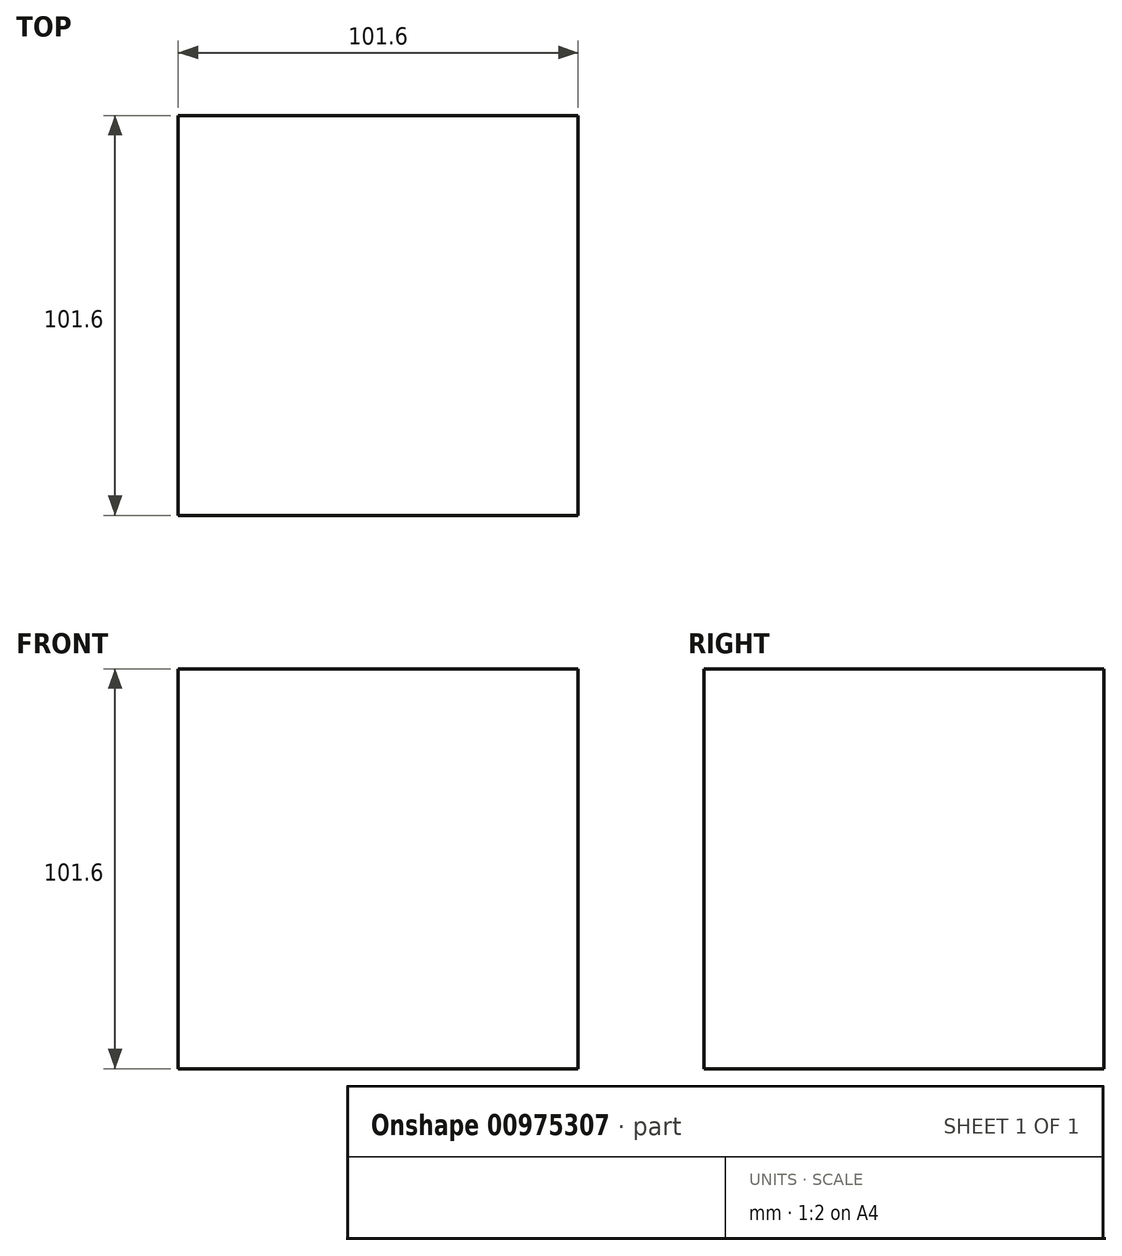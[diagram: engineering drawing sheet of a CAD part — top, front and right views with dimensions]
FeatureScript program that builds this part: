
annotation { "Feature Type Name" : "Feature", "Feature Type Description" : "" }
export const myFeature = defineFeature(function(context is Context, id is Id, definition is map)
    precondition{}
    {
        {
            var Q0;
            Q0=qCreatedBy(makeId("Top.planeOp"),FACE);
            var sketch = newSketch(context, id + "F0", { "sketchPlane" : qUnion([Q0])});
            skLineSegment(sketch, "E0.bottom", {"start": v(-80.82, 79.15) * mm, "end": v(20.78, 79.15) * mm});
            skLineSegment(sketch, "E0.top", {"start": v(-80.82, -22.45) * mm, "end": v(20.78, -22.45) * mm});
            skLineSegment(sketch, "E0.left", {"start": v(-80.82, 79.15) * mm, "end": v(-80.82, -22.45) * mm});
            skLineSegment(sketch, "E0.right", {"start": v(20.78, 79.15) * mm, "end": v(20.78, -22.45) * mm});
            skSolve(sketch);
        }
        {
            var Q0;
            Q0=makeQuery(id+"F0.imprint","IMPRINT",FACE,{"disambiguationData":[TD([[makeQuery(id+"F0.imprint","IMPRINT",EDGE,{"derivedFrom":sQuery(id+"F0.wireOp",EDGE,"E0.bottom")}),-1.0]])]});
            extrude(context, id + "F1", {"entities" : qUnion([Q0]), "depth" : 101.6 * mm, "offsetDistance" : 25.4 * mm});
        }
    });
